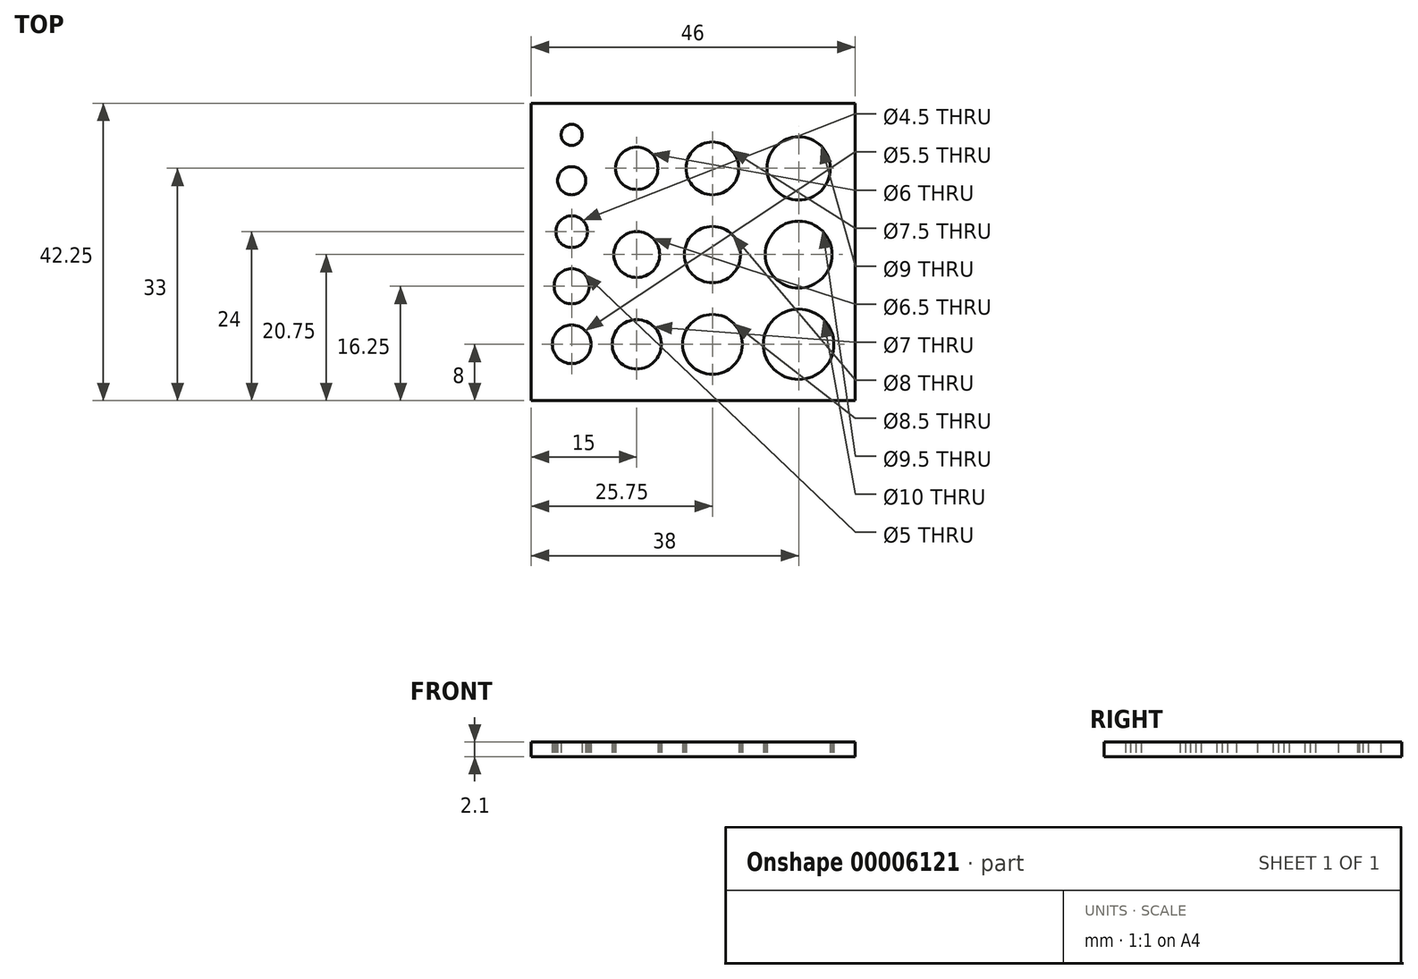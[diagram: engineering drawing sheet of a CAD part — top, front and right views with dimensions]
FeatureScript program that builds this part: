
annotation { "Feature Type Name" : "Feature", "Feature Type Description" : "" }
export const myFeature = defineFeature(function(context is Context, id is Id, definition is map)
    precondition{}
    {
        {
            var Q0;
            Q0=qCreatedBy(makeId("Top.planeOp"),FACE);
            var sketch = newSketch(context, id + "F0", { "sketchPlane" : qUnion([Q0])});
            skCircle(sketch, "E0", {"center": v(5.75, -4.5) * mm, "radius": 1.5 * mm});
            skCircle(sketch, "E1", {"center": v(5.75, -18.25) * mm, "radius": 2.25 * mm});
            skCircle(sketch, "E2", {"center": v(5.75, -34.25) * mm, "radius": 2.75 * mm});
            skCircle(sketch, "E3", {"center": v(15, -9.25) * mm, "radius": 3 * mm});
            skCircle(sketch, "E4", {"center": v(25.75, -9.25) * mm, "radius": 3.75 * mm});
            skCircle(sketch, "E5", {"center": v(38, -9.25) * mm, "radius": 4.5 * mm});
            skCircle(sketch, "E6", {"center": v(15, -21.5) * mm, "radius": 3.25 * mm});
            skCircle(sketch, "E7", {"center": v(15, -34.25) * mm, "radius": 3.5 * mm});
            skCircle(sketch, "E8", {"center": v(25.75, -21.5) * mm, "radius": 4 * mm});
            skCircle(sketch, "E9", {"center": v(25.75, -34.25) * mm, "radius": 4.25 * mm});
            skCircle(sketch, "E10", {"center": v(38, -21.5) * mm, "radius": 4.75 * mm});
            skCircle(sketch, "E11", {"center": v(38, -34.25) * mm, "radius": 5 * mm});
            skLineSegment(sketch, "E12.bottom", {"start": v(0, 0) * mm, "end": v(46, 0) * mm});
            skLineSegment(sketch, "E12.top", {"start": v(0, -42.25) * mm, "end": v(46, -42.25) * mm});
            skLineSegment(sketch, "E12.left", {"start": v(0, 0) * mm, "end": v(0, -42.25) * mm});
            skLineSegment(sketch, "E12.right", {"start": v(46, 0) * mm, "end": v(46, -42.25) * mm});
            skCircle(sketch, "E13", {"center": v(5.75, -11) * mm, "radius": 2 * mm});
            skCircle(sketch, "E14", {"center": v(5.75, -26) * mm, "radius": 2.5 * mm});
            skSolve(sketch);
        }
        {
            var Q0;
            Q0=qSketchRegion(id+"F0",true);
            extrude(context, id + "F1", {"entities" : qUnion([Q0]), "depth" : 2.1 * mm});
        }
    });
